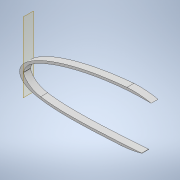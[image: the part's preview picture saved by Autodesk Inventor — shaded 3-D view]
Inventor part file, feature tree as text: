
AUTODESK INVENTOR PART (.ipt)
format: ipt  version: 2022.1 (Build 261234020, 234B)  size: 557,568 bytes
history: native  units: mm
features: sketch x7, extrude x6, thicken_offset x4, projected_geometry x3, shell x1, plane x1, other x1, fillet x1
ambient origin geometry x8: Origin, YZ Plane, XZ Plane, XY Plane, X Axis, Y Axis, Z Axis, Center Point
bodies: Solid1 (feature_tree)
feature tree (24):
  extrude  "Extrusion1"  Depth=3.0mm
  shell  "Shell1"  Thickness=1.0mm
  thicken_offset  "Thicken1"
  extrude  "Extrusion27"  TaperAngle=0.0deg  [1 undecoded]
  thicken_offset  "Thicken3"
  extrude  "Extrusion29"  Depth=20.0mm
  plane  "Work Plane5"
  other  "Bend Part2"
  thicken_offset  "Thicken5"
  extrude  "Extrusion30"  Depth=10.0mm TaperAngle=0.0deg
  extrude  "Extrusion31"  Depth=1.0mm
  thicken_offset  "Thicken6"
  extrude  "Extrusion32"  Depth=100.0mm
  fillet  "Fillet6"  Radius=5.0mm
  sketch  "Sketch3"  dims[d0=10.0mm d1=0.0mm d2=3.0mm d159=1.0mm d160=2.0mm]
  sketch  "Sketch48"  dims[d236=190.0mm d237=0.0mm d238=0.0mm]
  sketch  "Sketch55"  dims[d249=2.0mm d250=1.0mm d254=20.0mm]
  projected_geometry  "Projected Loop32"
  sketch  "Sketch57"  dims[d255=8.0mm d256=10.0mm d257=0.0mm]
  sketch  "Sketch58"  dims[d262=10.0mm d263=0.349066mm d264=1.0mm]
  projected_geometry  "Projected Loop34"
  sketch  "Sketch59"  dims[d265=1.0mm d268=100.0mm d269=5.0mm]
  sketch  "Sketch60"  dims[d270=10.0mm d271=0.0mm d272=150.0mm d273=100.0mm d274=0.0mm d275=2.5mm d276=2.0mm d277=3.0mm d278=300.0mm d279=10.0mm d280=0.0mm d281=100.0mm d282=20.0mm d284=10.0mm d283=0.0mm]
  projected_geometry  "Projected Loop35"
note: 1 required parameter value undecoded (feature->parameter linkage not recoverable at this tier; creation-order binding heuristic only, values carry confidence <= 0.55)
